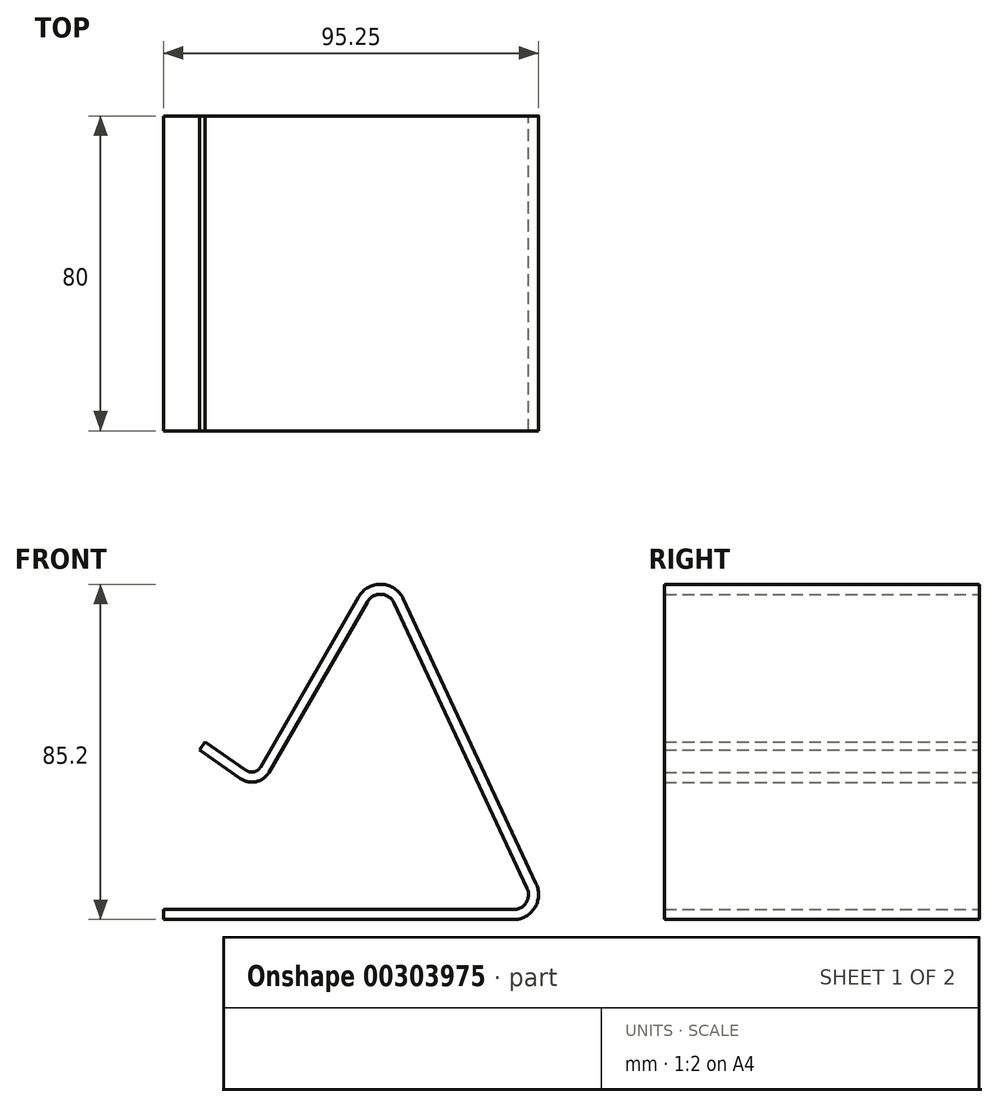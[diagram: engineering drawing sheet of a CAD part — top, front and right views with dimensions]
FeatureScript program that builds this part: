
annotation { "Feature Type Name" : "Feature", "Feature Type Description" : "" }
export const myFeature = defineFeature(function(context is Context, id is Id, definition is map)
    precondition{}
    {
        {
            var Q0;
            Q0=qCreatedBy(makeId("Front.planeOp"),FACE);
            var sketch = newSketch(context, id + "F0", { "sketchPlane" : qUnion([Q0])});
            skLineSegment(sketch, "E0", {"start": v(0, 0) * mm, "end": v(88.9, 0) * mm});
            skLineSegment(sketch, "E1", {"start": v(92.35, 5.42) * mm, "end": v(58.54, 77.92) * mm});
            skLineSegment(sketch, "E2", {"start": v(51.8, 78.22) * mm, "end": v(26.8, 34.92) * mm});
            skLineSegment(sketch, "E3.1", {"start": v(24.6, 36.19) * mm, "end": v(49.6, 79.49) * mm});
            skLineSegment(sketch, "E3.2", {"start": v(94.66, 6.5) * mm, "end": v(60.85, 79) * mm});
            skLineSegment(sketch, "E3.3", {"start": v(0, -2.54) * mm, "end": v(88.9, -2.54) * mm});
            skLineSegment(sketch, "E4", {"start": v(10.53, 42.66) * mm, "end": v(9.07, 40.58) * mm});
            skLineSegment(sketch, "E5", {"start": v(0, -2.54) * mm, "end": v(0, 0) * mm});
            skPoint(sketch, "E6.visualSharp", {"position": v(94.88, 0) * mm});
            skArc(sketch, "E6.filletArc", {"start": v(88.9, 0) * mm, "mid": v(92.11, 1.76) * mm, "end": v(92.35, 5.42) * mm});
            skPoint(sketch, "E7.visualSharp", {"position": v(-826.19, 0) * mm});
            skArc(sketch, "E8", {"start": v(94.66, 6.5) * mm, "mid": v(94.26, 0.4) * mm, "end": v(88.9, -2.54) * mm});
            skArc(sketch, "E9", {"start": v(51.8, 78.22) * mm, "mid": v(55.26, 80.12) * mm, "end": v(58.54, 77.92) * mm});
            skArc(sketch, "E10", {"start": v(49.6, 79.49) * mm, "mid": v(55.37, 82.66) * mm, "end": v(60.85, 79) * mm});
            skLineSegment(sketch, "E11", {"start": v(10.53, 42.66) * mm, "end": v(20.93, 35.38) * mm});
            skLineSegment(sketch, "E12", {"start": v(9.07, 40.58) * mm, "end": v(19.48, 33.3) * mm});
            skArc(sketch, "E13", {"start": v(20.93, 35.38) * mm, "mid": v(22.94, 34.98) * mm, "end": v(24.6, 36.19) * mm});
            skArc(sketch, "E14", {"start": v(19.48, 33.3) * mm, "mid": v(23.5, 32.5) * mm, "end": v(26.8, 34.92) * mm});
            skSolve(sketch);
        }
        {
            var Q0;
            Q0=makeQuery(id+"F0.imprint","IMPRINT",FACE,{"disambiguationData":[TD([[makeQuery(id+"F0.imprint","IMPRINT",EDGE,{"derivedFrom":sQuery(id+"F0.wireOp",EDGE,"E0")}),-1.0]])]});
            extrude(context, id + "F1", {"entities" : qUnion([Q0]), "depth" : 80 * mm});
        }
    });
